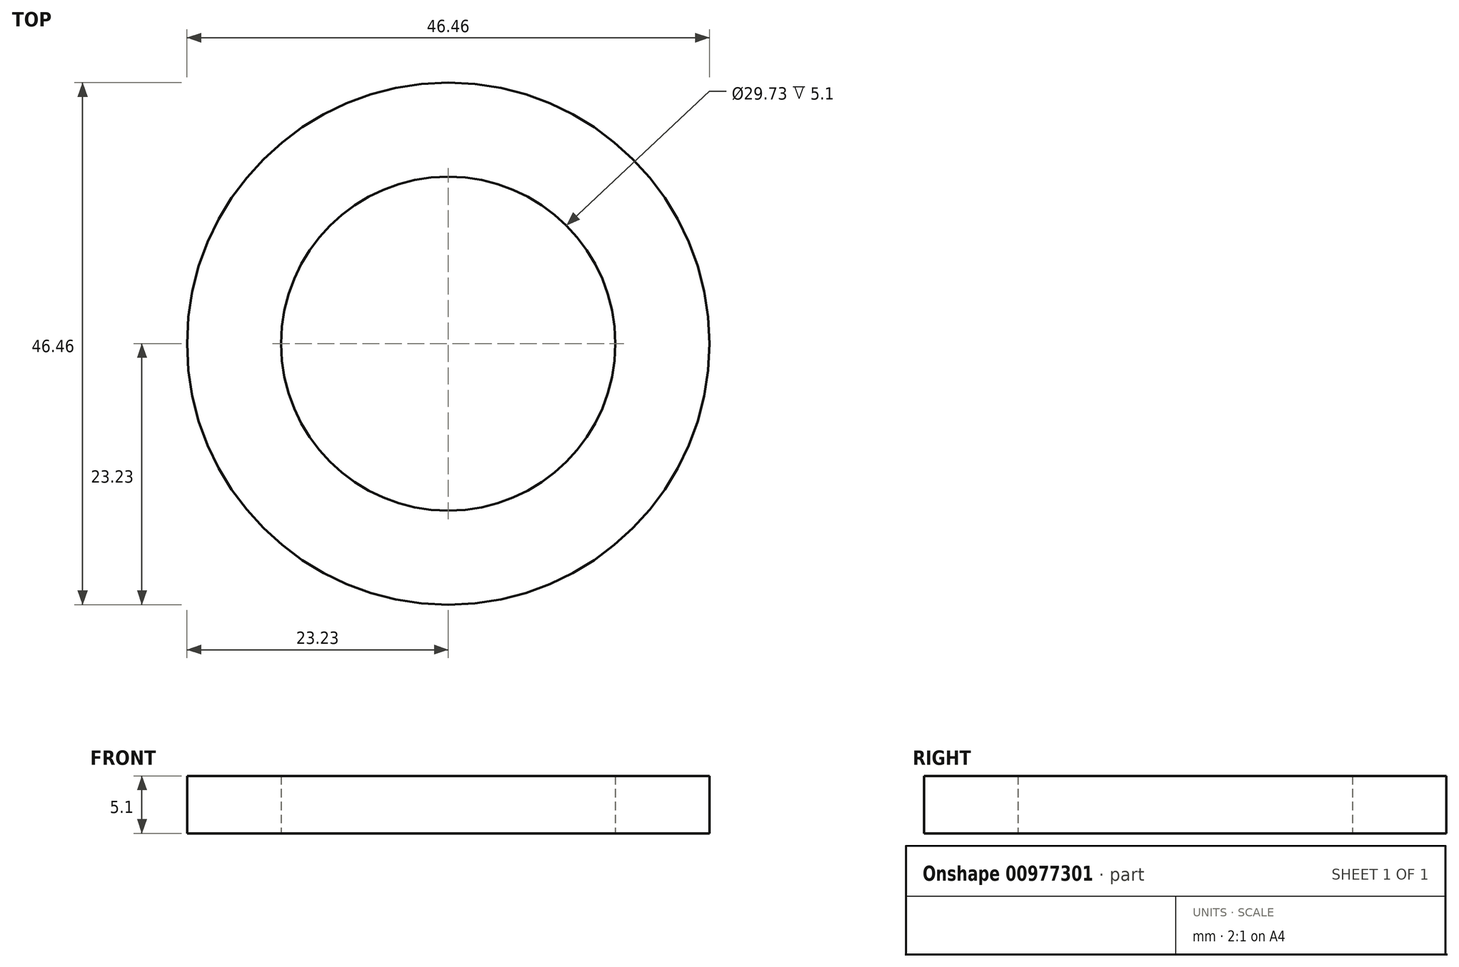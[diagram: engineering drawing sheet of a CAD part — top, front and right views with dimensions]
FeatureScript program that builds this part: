
annotation { "Feature Type Name" : "Feature", "Feature Type Description" : "" }
export const myFeature = defineFeature(function(context is Context, id is Id, definition is map)
    precondition{}
    {
        {
            var Q0;
            Q0=qCreatedBy(makeId("Top.planeOp"),FACE);
            var sketch = newSketch(context, id + "F0", { "sketchPlane" : qUnion([Q0])});
            skCircle(sketch, "E0", {"center": v(0, 0) * mm, "radius": 23.23 * mm});
            skCircle(sketch, "E1", {"center": v(0, 0) * mm, "radius": 14.87 * mm});
            skArc(sketch, "E2", {"start": v(1.62, 23.17) * mm, "mid": v(-2.32, 18.97) * mm, "end": v(1.62, 14.78) * mm});
            skArc(sketch, "E3", {"start": v(1.62, 22.76) * mm, "mid": v(-1.91, 18.97) * mm, "end": v(1.62, 15.2) * mm});
            skArc(sketch, "E4.MirrorCS", {"start": v(1.62, -23.32) * mm, "mid": v(-2.32, -19.12) * mm, "end": v(1.62, -14.93) * mm});
            skArc(sketch, "E5.MirrorCS", {"start": v(1.62, -22.9) * mm, "mid": v(-1.91, -19.12) * mm, "end": v(1.62, -15.34) * mm});
            skLineSegment(sketch, "E6.MirrorCS", {"start": v(1.62, -24.3) * mm, "end": v(1.62, -13.92) * mm, "construction": true});
            skArc(sketch, "E7.MirrorCS", {"start": v(21.75, 11.55) * mm, "mid": v(20.09, 6.04) * mm, "end": v(14.48, 7.35) * mm});
            skArc(sketch, "E8.MirrorCS", {"start": v(21.4, 11.34) * mm, "mid": v(19.88, 6.4) * mm, "end": v(14.84, 7.56) * mm});
            skLineSegment(sketch, "E9.MirrorCS", {"start": v(22.6, 12.04) * mm, "end": v(13.6, 6.85) * mm, "construction": true});
            skArc(sketch, "E10.MirrorCS", {"start": v(-18.51, -11.7) * mm, "mid": v(-12.9, -13.01) * mm, "end": v(-11.24, -7.5) * mm});
            skLineSegment(sketch, "E11.MirrorCS", {"start": v(-19.37, -12.2) * mm, "end": v(-10.37, -7) * mm, "construction": true});
            skLineSegment(sketch, "E12.MirrorCS", {"start": v(25.85, -0.07) * mm, "end": v(15.46, -0.07) * mm, "construction": true});
            skArc(sketch, "E13.MirrorCS", {"start": v(24.45, -0.07) * mm, "mid": v(20.67, -3.6) * mm, "end": v(16.89, -0.07) * mm});
            skArc(sketch, "E14.MirrorCS", {"start": v(24.86, -0.07) * mm, "mid": v(20.67, -4.02) * mm, "end": v(16.47, -0.07) * mm});
            skArc(sketch, "E15.MirrorCS", {"start": v(-21.21, -0.07) * mm, "mid": v(-17.43, -3.6) * mm, "end": v(-13.65, -0.07) * mm});
            skArc(sketch, "E16.MirrorCS", {"start": v(-21.62, -0.07) * mm, "mid": v(-17.43, -4.02) * mm, "end": v(-13.23, -0.07) * mm});
            skLineSegment(sketch, "E17.MirrorCS", {"start": v(-22.61, -0.07) * mm, "end": v(-12.22, -0.07) * mm, "construction": true});
            skLineSegment(sketch, "E18.MirrorCS", {"start": v(-10.5, 20.91) * mm, "end": v(-5.3, 11.91) * mm, "construction": true});
            skArc(sketch, "E19.MirrorCS", {"start": v(-9.8, 19.7) * mm, "mid": v(-10.96, 14.66) * mm, "end": v(-6.01, 13.15) * mm});
            skArc(sketch, "E20.MirrorCS", {"start": v(-10, 20.06) * mm, "mid": v(-11.32, 14.45) * mm, "end": v(-5.8, 12.79) * mm});
            skArc(sketch, "E21.MirrorCS", {"start": v(13.24, -20.2) * mm, "mid": v(7.73, -18.54) * mm, "end": v(9.05, -12.94) * mm});
            skArc(sketch, "E22.MirrorCS", {"start": v(13.03, -19.85) * mm, "mid": v(8.09, -18.34) * mm, "end": v(9.25, -13.3) * mm});
            skLineSegment(sketch, "E23.MirrorCS", {"start": v(13.74, -21.06) * mm, "end": v(8.54, -12.06) * mm, "construction": true});
            skLineSegment(sketch, "E24.MirrorCS", {"start": v(-10.5, -21.06) * mm, "end": v(-5.3, -12.06) * mm, "construction": true});
            skArc(sketch, "E25.MirrorCS", {"start": v(-9.8, -19.85) * mm, "mid": v(-10.96, -14.8) * mm, "end": v(-6.01, -13.3) * mm});
            skArc(sketch, "E26.MirrorCS", {"start": v(-10, -20.2) * mm, "mid": v(-11.32, -14.6) * mm, "end": v(-5.8, -12.94) * mm});
            skArc(sketch, "E27.MirrorCS", {"start": v(13.03, 19.7) * mm, "mid": v(8.09, 18.19) * mm, "end": v(9.25, 13.15) * mm});
            skArc(sketch, "E28.MirrorCS", {"start": v(13.24, 20.06) * mm, "mid": v(7.73, 18.4) * mm, "end": v(9.05, 12.79) * mm});
            skLineSegment(sketch, "E29.MirrorCS", {"start": v(13.74, 20.91) * mm, "end": v(8.54, 11.91) * mm, "construction": true});
            skLineSegment(sketch, "E30.MirrorCS", {"start": v(-19.37, 12.04) * mm, "end": v(-10.37, 6.85) * mm, "construction": true});
            skArc(sketch, "E31.MirrorCS", {"start": v(-18.51, 11.55) * mm, "mid": v(-16.85, 6.04) * mm, "end": v(-11.24, 7.35) * mm});
            skArc(sketch, "E32.MirrorCS", {"start": v(-18.15, 11.34) * mm, "mid": v(-16.64, 6.4) * mm, "end": v(-11.6, 7.56) * mm});
            skLineSegment(sketch, "E33.MirrorCS", {"start": v(22.6, -12.2) * mm, "end": v(13.6, -7) * mm, "construction": true});
            skArc(sketch, "E34.MirrorCS", {"start": v(21.4, -11.5) * mm, "mid": v(16.35, -12.66) * mm, "end": v(14.84, -7.7) * mm});
            skArc(sketch, "E35.MirrorCS", {"start": v(21.75, -11.7) * mm, "mid": v(16.15, -13.01) * mm, "end": v(14.48, -7.5) * mm});
            skArc(sketch, "E36.MirrorCS", {"start": v(-18.15, -11.5) * mm, "mid": v(-13.11, -12.66) * mm, "end": v(-11.6, -7.7) * mm});
            skLineSegment(sketch, "E37", {"start": v(1.62, 23.6) * mm, "end": v(1.62, 13.88) * mm, "construction": true});
            skSolve(sketch);
        }
        {
            var Q0;
            {var subQ8=sQuery(id+"F0.wireOp",EDGE,"E0");Q0=makeQuery(id+"F0.imprint","IMPRINT",FACE,{"disambiguationData":[TD([[makeQuery(id+"F0.imprint","IMPRINT",EDGE,{"disambiguationData":[TD([[makeQuery(id+"F0.imprint","IMPRINT",VERTEX,{"derivedFrom":subQ8}),-1.0]])],"derivedFrom":subQ8}),1.0]])]});}
            extrude(context, id + "F1", {"entities" : qUnion([Q0]), "depth" : 5.1 * mm, "offsetDistance" : 25 * mm});
        }
    });
